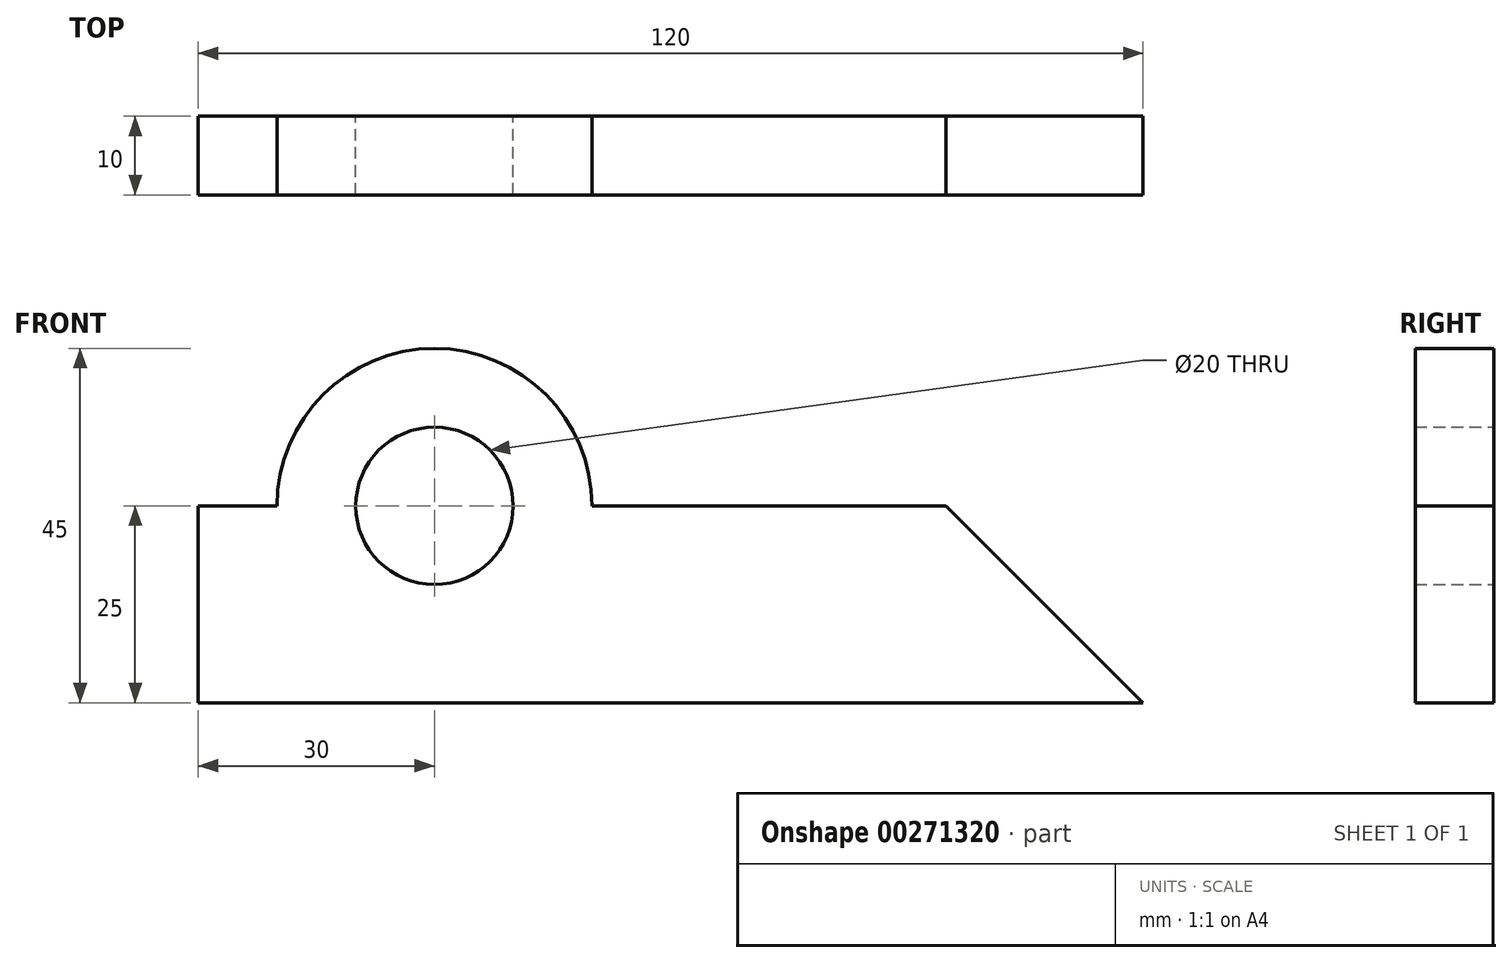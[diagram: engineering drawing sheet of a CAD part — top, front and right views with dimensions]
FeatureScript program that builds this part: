
annotation { "Feature Type Name" : "Feature", "Feature Type Description" : "" }
export const myFeature = defineFeature(function(context is Context, id is Id, definition is map)
    precondition{}
    {
        {
            var Q0;
            Q0=qCreatedBy(makeId("Front.planeOp"),FACE);
            var sketch = newSketch(context, id + "F0", { "sketchPlane" : qUnion([Q0])});
            skLineSegment(sketch, "E0", {"start": v(0, 0) * mm, "end": v(120, 0) * mm});
            skLineSegment(sketch, "E1", {"start": v(120, 0) * mm, "end": v(95, 25) * mm});
            skLineSegment(sketch, "E2", {"start": v(95, 25) * mm, "end": v(50, 25) * mm});
            skLineSegment(sketch, "E3", {"start": v(0, 0) * mm, "end": v(0, 25) * mm});
            skLineSegment(sketch, "E4", {"start": v(0, 25) * mm, "end": v(10, 25) * mm});
            skArc(sketch, "E5", {"start": v(50, 25) * mm, "mid": v(30, 45) * mm, "end": v(10, 25) * mm});
            skCircle(sketch, "E6", {"center": v(30, 25) * mm, "radius": 10 * mm});
            skSolve(sketch);
        }
        {
            var Q0;
            Q0 = qSketchRegion(id + "F0", true);
            extrude(context, id + "F1", {"entities" : qUnion([Q0]), "depth" : 10 * mm});
        }
    });
